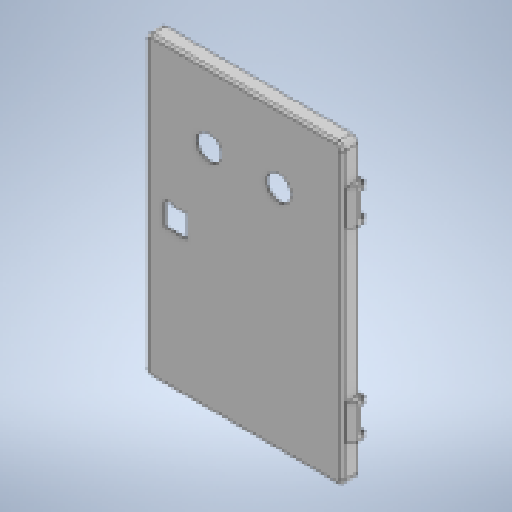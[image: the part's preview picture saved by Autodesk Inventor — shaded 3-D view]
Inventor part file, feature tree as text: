
AUTODESK INVENTOR PART (.ipt)
format: ipt  version: 2025.2 (Build 292293000, 293)  size: 436,736 bytes
history: native  units: mm
features: other x28, sketch x22, extrude x13, revolve x9, thread x1
ambient origin geometry x8: Origin, YZ Plane, XZ Plane, XY Plane, X Axis, Y Axis, Z Axis, Center Point
bodies: Solid1 (feature_tree)
feature tree (73):
  extrude  "Extrusion1"  Depth=286.0mm TaperAngle=0.0deg
  extrude  "Extrusion2"  TaperAngle=90.0deg  [1 undecoded]
  revolve  "Revolution1"  Angle=90.0deg
  revolve  "Revolution2"  Angle=90.0deg
  revolve  "Revolution3"  Angle=90.0deg
  revolve  "Revolution4"  [1 undecoded]
  extrude  "Extrusion3"  Depth=188.0mm TaperAngle=0.0deg
  revolve  "Revolution5"  Angle=360.0deg
  revolve  "Revolution6"  [1 undecoded]
  revolve  "Revolution7"  [1 undecoded]
  revolve  "Revolution8"  [1 undecoded]
  extrude  "Extrusion4"  Depth=80.0mm
  extrude  "Extrusion5"  Depth=25.0mm
  extrude  "Extrusion6"  Depth=25.0mm
  extrude  "Extrusion7"  Depth=35.0mm
  revolve  "Revolution9"  [1 undecoded]
  thread  "Thread1"  [1 undecoded]
  extrude  "Extrusion8"  [1 undecoded]
  extrude  "Extrusion9"  [1 undecoded]
  extrude  "Extrusion10"  [1 undecoded]
  extrude  "Extrusion11"  [1 undecoded]
  other  "DECKEL_XY"
  other  "DECKEL_YZ"
  other  "DECKEL_ZX"
  other  "DECKEL_X"
  other  "DECKEL_Y"
  other  "DECKEL_Z"
  other  "DECKEL_Center"
  other  "VB_XY"
  other  "VB_YZ"
  other  "VB_ZX"
  other  "VB_X"
  other  "VB_Y"
  other  "VB_Z"
  other  "VB_Center"
  other  "to_HINGE_XY"
  other  "to_HINGE_YZ"
  other  "to_HINGE_ZX"
  other  "to_HINGE_X"
  other  "to_HINGE_Y"
  other  "to_HINGE_Z"
  other  "to_HINGE_Center"
  other  "to_HINGE_1_XY"
  other  "to_HINGE_1_YZ"
  other  "to_HINGE_1_ZX"
  other  "to_HINGE_1_X"
  other  "to_HINGE_1_Y"
  other  "to_HINGE_1_Z"
  other  "to_HINGE_1_Center"
  extrude  "Extrusion12"  [1 undecoded]
  extrude  "Extrusion13"  [1 undecoded]
  sketch  "Skizze_2"  dims[d4=90.0deg d5=90.0deg]
  sketch  "Skizze_4"  dims[d8=176.5mm d9=0.0mm d10=90.0deg]
  sketch  "Skizze_5"  dims[d13=90.0deg d14=276.5mm d15=0.0mm]
  sketch  "Skizze_6"  dims[d20=1.25mm d21=0.0mm d22=360.0deg]
  sketch  "Skizze_7"  dims[d27=35.0mm d28=0.0mm d29=25.0mm d30=0.0mm]
  sketch  "Skizze_8"  dims[d31=25.0mm d32=0.0mm d33=0.0mm]
  sketch  "Skizze_29"  dims[d47=10.0mm d48=0.0mm]
  sketch  "Skizze_30"
  sketch  "Skizze_31"
  sketch  "Skizze_32"
  sketch  "Skizze_33"
  sketch  "Skizze_34"
  sketch  "Sketch_5"  dims[d16=288.0mm d17=0.0mm d18=188.0mm d19=0.0mm]
  sketch  "Sketch_6"  dims[d23=7.1865mm d24=0.0mm d25=35.0mm d26=0.0mm]
  sketch  "Sketch_3"  dims[d6=90.0deg d7=90.0deg]
  sketch  "Sketch_1"  dims[d0=186.0mm d1=0.0mm d2=286.0mm d3=0.0mm]
  sketch  "Sketch_4"  dims[d11=90.0deg d12=90.0deg]
  sketch  "Sketch_10"  dims[d36=35.0mm d37=25.0mm]
  sketch  "Sketch_9"  dims[d34=0.0mm d35=80.0mm]
  sketch  "Sketch_11"  dims[d38=10.0mm d39=0.0mm d41=25.0mm]
  sketch  "Sketch21"  dims[d42=80.0mm d43=35.0mm]
  sketch  "Sketch25"  dims[d44=25.0mm d45=35.0mm d46=80.0mm]
note: 13 required parameter values undecoded (feature->parameter linkage not recoverable at this tier; creation-order binding heuristic only, values carry confidence <= 0.55)